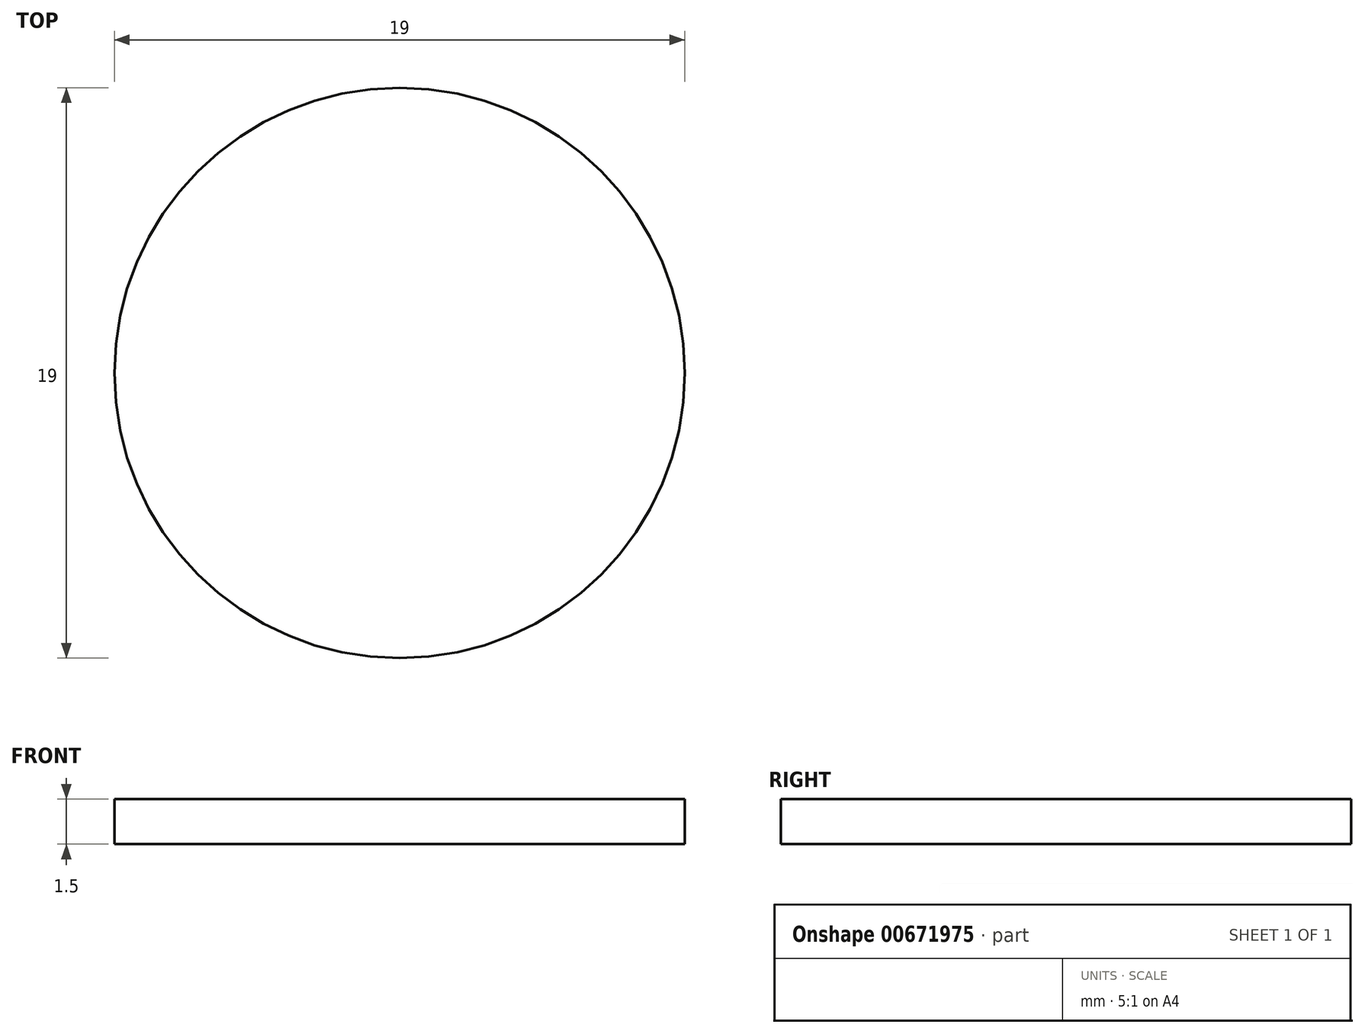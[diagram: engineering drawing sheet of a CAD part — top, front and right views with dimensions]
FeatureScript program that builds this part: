
annotation { "Feature Type Name" : "Feature", "Feature Type Description" : "" }
export const myFeature = defineFeature(function(context is Context, id is Id, definition is map)
    precondition{}
    {
        {
            var Q0;
            Q0=qCreatedBy(makeId("Top.planeOp"),FACE);
            var sketch = newSketch(context, id + "F0", { "sketchPlane" : qUnion([Q0])});
            skCircle(sketch, "E0", {"center": v(0, 0) * mm, "radius": 9.5 * mm});
            skSolve(sketch);
        }
        {
            var Q0;
            Q0 = qSketchRegion(id + "F0", true);
            extrude(context, id + "F1", {"entities" : qUnion([Q0]), "depth" : 1.5 * mm, "offsetDistance" : 25 * mm});
        }
    });
